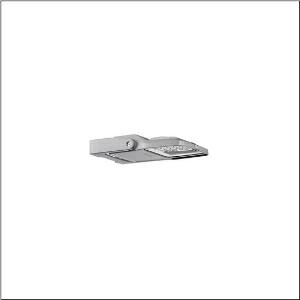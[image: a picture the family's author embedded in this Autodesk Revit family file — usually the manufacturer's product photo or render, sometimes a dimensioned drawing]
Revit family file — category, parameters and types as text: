
# Revit family: floodlight_fl_21_iq_micro___pl61_5xa7762a4c2a_69cd
name_source: partatom
category: Lighting Fixtures
units: mm (PartAtom-declared; Revit-internal decimal feet)

## family parameters
Cut with Voids When Loaded = No
Host = Face
Light Source = No
Part Type = Normal
Room Calculation Point = No
Round Connector Dimension = Use Diameter
Shared = No

## types (1)
- --- (1 x LED, 3030 lm, 23.1 W, 4000K)
    Apparent Load = 23 VA
    CIE Flux Codes = 33 65 98 100 100
    Color Rendering = 70
    Color Temperature = 4000K
    Default Elevation = 1800 mm
    Description = Floodlight FL 21 iQ micro, floodlight, primary light control with lens, of PMMA, primary optical cover: protective disc, of toughened safety glass, transparent, light distribution: PL61, light emission: direct distribution, installation type: surface-mounted, LED, High Power LED, rated luminous flux: 3.030lm, luminous efficacy: 131lm/W, light colour: 740, colour temperature: 4000K, control: Auto-Match, Temp-Guard, Night-Set, Smart-Wire, Desk-Remote (wireless, voltage-free reading and setting of iQ features in the workshop via application-optimized NFC function/RFID function), optimised constant luminous flux control (CLO 2.0), Street-Remote, with terminal, 6-pole, mains connection: 220..240V, AC, 50/60Hz, start of lifetime: 23W, end of service life: 24W, reduction: 11W, luminaire housing, of diecast aluminium, powder-coated, Siteco® metallic grey (DB 702S), corrosivity category C5 mid according to DIN EN ISO 12944, sealing non-destructively replaceable, design bracket, of diecast aluminium, powder-coated, Siteco® metallic grey (DB 702S), protection rating (complete): IP66, insulation class (complete): insulation class II (safety insulation), certification: CE, ENEC, VDE, protection symbol: D, impact resistance: IK07, permissible operating ambient temperature: -40..+40°C, permissible operating ambient temperature for outdoor applications: -40..+50°C, standard: DIN EN 12944, LABS conformity tested according to VDMA 24364:2018-05, packaging unit: 1 piece

Light Distribution: PL61
    Height = 65 mm
    Lamp = 1 x LED
    Lamp Light Flux = 3030 lm
    Lamp Power = 23.1 W
    Lamp count = 1
    Length = 312 mm
    Luminous efficacy = 131 lm/W
    Manufacturer = Siteco
    ModVariant = No
    Model = 5XA7762A4C2A
    Mounting Place = Wall
    Mounting Type = Surface mounted
    Number of Poles = 1
    OnlyDefault = Yes
    Power Factor = 1
    Product Name = Floodlight FL 21 iQ micro | PL61
    Product group = floodlight | wall mounted
    ProductGroupID = 2001
    Protection Class = Protection class II
    Protection Degree = IP 66
    RLX_Detail_Level = 1
    RLX_Emergency_Light_Flux = 0 lm
    RLX_Emergency_Type = 0
    RLX_Emergency_Type_DB = No
    RlxData = <blob elided: 97513 chars, md5=32725564>
    Socket = socket
    Standby Power = 0 W
    System Light Flux = 3030 lm
    System Power = 23 W
    Type Comments = factory setting: luminous flux: 100 % | dim-lin: 254 | 455 mA
    Type Image = l_1006878.jpg
    URL = http://relux.com
    VarID = @adj_146941
    Voltage = 0 V
    Weight = 0.00 kg
    Width = 230 mm

## geometry (parser evidence)
native form markers: Blend x4, Sweep x13
no freeform markers — native parametric forms only
